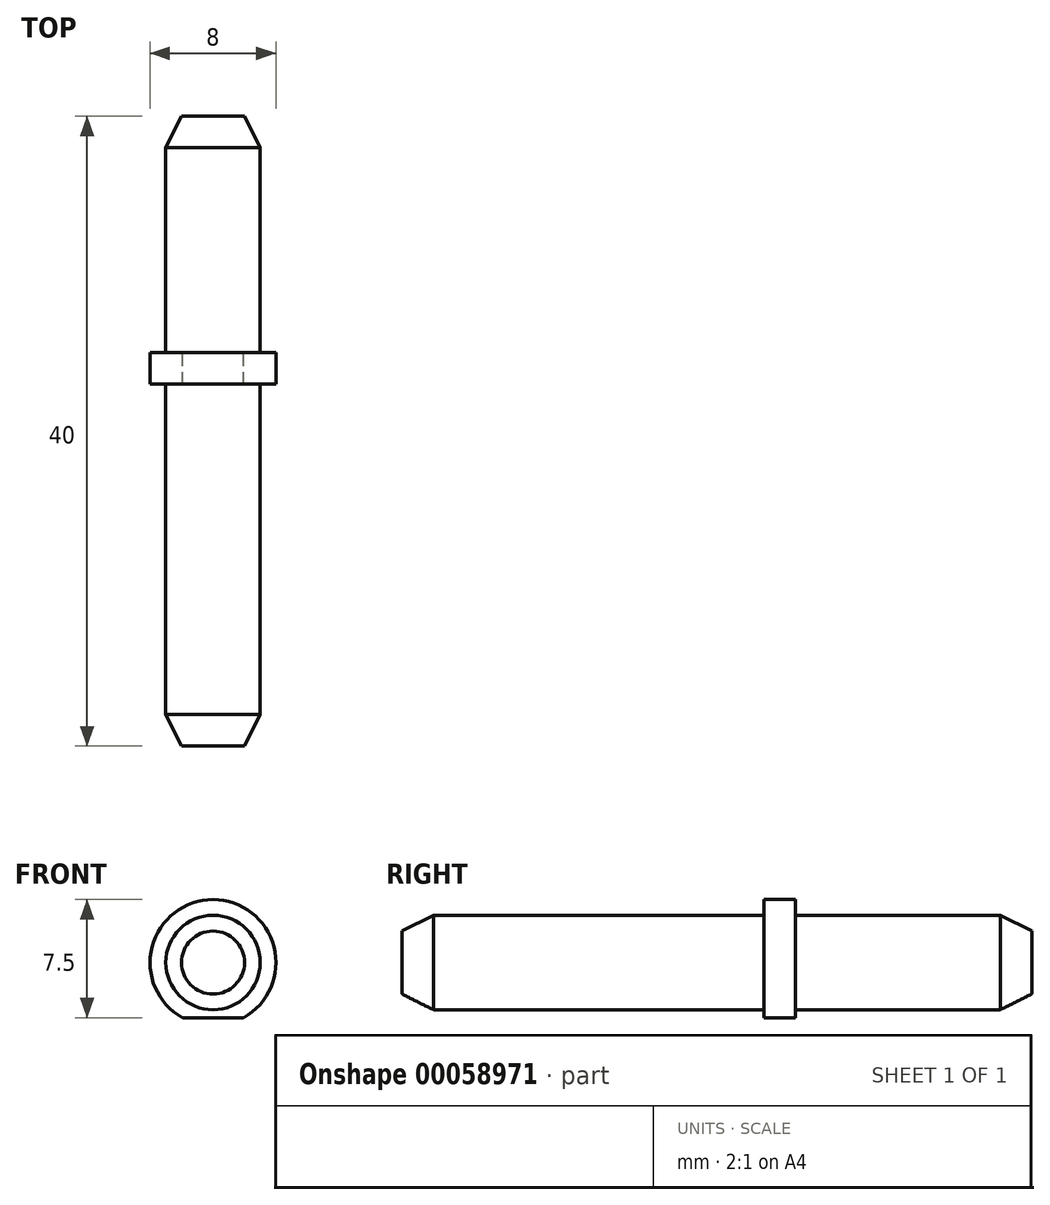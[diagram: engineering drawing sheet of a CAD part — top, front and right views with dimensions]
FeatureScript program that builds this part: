
annotation { "Feature Type Name" : "Feature", "Feature Type Description" : "" }
export const myFeature = defineFeature(function(context is Context, id is Id, definition is map)
    precondition{}
    {
        {
            var Q0;
            Q0=qCreatedBy(makeId("Front.planeOp"),FACE);
            var sketch = newSketch(context, id + "F0", { "sketchPlane" : qUnion([Q0])});
            skCircle(sketch, "E0", {"center": v(0, 0) * mm, "radius": 3 * mm});
            skCircle(sketch, "E1", {"center": v(0, 0) * mm, "radius": 4 * mm});
            skLineSegment(sketch, "E2", {"start": v(-4.44, -4) * mm, "end": v(4.42, -4) * mm, "construction": true});
            skLineSegment(sketch, "E3.0", {"start": v(-4.44, -3.5) * mm, "end": v(4.42, -3.5) * mm, "construction": true});
            skLineSegment(sketch, "E4", {"start": v(-1.94, -3.5) * mm, "end": v(1.94, -3.5) * mm});
            skSolve(sketch);
        }
        {
            var Q0;
            Q0=makeQuery(id+"F0.imprint","IMPRINT",FACE,{"disambiguationData":[TD([[makeQuery(id+"F0.imprint","IMPRINT",EDGE,{"derivedFrom":sQuery(id+"F0.wireOp",EDGE,"E0")}),1.0]])]});
            extrude(context, id + "F1", {"entities" : qUnion([Q0]), "depth" : 25 * mm});
        }
        {
            var Q0;
            Q0=makeQuery(id+"F0.imprint","IMPRINT",FACE,{"disambiguationData":[TD([[makeQuery(id+"F0.imprint","IMPRINT",EDGE,{"derivedFrom":sQuery(id+"F0.wireOp",EDGE,"E0")}),-1.0]])]});
            extrude(context, id + "F2", {"entities" : qUnion([Q0]), "operationType" : NewBodyOperationType.ADD, "depth" : 2 * mm});
        }
        {
            var Q0;
            Q0=makeQuery(id+"F0.imprint","IMPRINT",FACE,{"disambiguationData":[TD([[makeQuery(id+"F0.imprint","IMPRINT",EDGE,{"derivedFrom":sQuery(id+"F0.wireOp",EDGE,"E0")}),1.0]])]});
            extrude(context, id + "F3", {"entities" : qUnion([Q0]), "operationType" : NewBodyOperationType.ADD, "oppositeDirection" : true, "depth" : 15 * mm});
        }
        {
            var Q0;
            Q0=makeQuery(id+"F3.opExtrude","CAP_EDGE",EDGE,{"disambiguationData":[OSD([sQuery(id+"F0.wireOp",EDGE,"E0")])],"isStart":false});
            chamfer(context, id + "F4", {"entities" : qUnion([Q0]), "chamferType" : ChamferType.TWO_OFFSETS, "width1" : 2 * mm, "oppositeDirection" : false, "width2" : 1 * mm, "tangentPropagation" : true});
        }
        {
            var Q0;
            Q0=makeQuery(id+"F1.opExtrude","CAP_EDGE",EDGE,{"disambiguationData":[OSD([sQuery(id+"F0.wireOp",EDGE,"E0")])],"isStart":false});
            chamfer(context, id + "F5", {"entities" : qUnion([Q0]), "chamferType" : ChamferType.TWO_OFFSETS, "width1" : 1 * mm, "oppositeDirection" : false, "width2" : 2 * mm, "tangentPropagation" : true});
        }
    });
